# Revit family: CONV_Wexiodisk_Dishwasher_WD-4S
name_source: partatom
category: Specialty Equipment
revit_build: Autodesk Revit 2016 (Build: 20150714_1515(x64)
units: mm (PartAtom-declared; Revit-internal decimal feet)

## family parameters
Always vertical = Yes
Cut with Voids When Loaded = No
OmniClass Number = 23.45.30.14.11
OmniClass Title = Commercial Dishwashers
Part Type = Normal
Room Calculation Point = No
Round Connector Dimension = Use Diameter
Shared = No
Work Plane-Based = No

## types (1)
- WD-4S
    AssetType = Fixed
    BIMObjectName = CONV_Wexiodisk_Dishwasher_WD-4S
    BasketSize = 500x500mm
    BoosterHeater(230V) = 2800 W
    BoosterHeater(400V) = 4200 W
    BoosterPump = 370 W
    Brand = Wexiodisk
    CapacityBasketsPerHour = 50
    Category = Under-counter dishwashers
    ColdWaterConnection(5-12°C)(ExternalThread) = R3/4"
    Color = Grey
    ConvergoRefNr = 0100-1703-0001-SE
    Cost = 0 $
    DishwasherMainMaterial = Stainless Steel
    DishwasherSecondaryMaterial = Black Plastic
    DrainConnectionHose = 22.00 mm
    DrainPump = 40 W
    DurationUnit = Year
    ElectricalDeviceNominalPower = 0 W
    ExpiringDate = 12/2018
    FloorDrain = 1.0 L/s
    HasProtectiveEarth = No
    HeatLoadToRoomLatent = 500 W
    HeatLoadToRoomSensible = 1200 W
    HeatLoadToRoomTotal = 1700 W
    HeatRecoveryFan = 10 W
    HotWaterConnection(55-70°C)(ExternalThread) = R3/4"
    IP_Code = 44
    IfcExportAs = NOTDEFINED
    IfcExportType = IfcFurnitureType
    MainFuse(230V-3N) = 4 A
    MainFuse(400V-3N) = 16 A
    ManufacterURL = https://www.wexiodisk.com
    Manufacturer = Wexiodisk
    ManufacturerName = Wexiodisk
    Material = Stainless Steel
    MaximumSurfaceTemperature = 35 °C
    Model = WD-4S
    NBSDescription = Commercial undercounter dishwashers
    NBSReference = 45-35-15/424
    Name = Dishwasher_WD-4S
    NominalCurrent = 0 A
    NominalDepth = 656 mm  [stored 2.15223 ft]
    NominalFrequencyRange = 0 Hz
    NominalHeight = 820 mm  [stored 2.69029 ft]
    NominalVoltage = 0 V
    NominalWidth = 598 mm  [stored 1.96194 ft]
    NumberOfPoles = 0
    PhaseAngle = 0.00°
    Revision = 2
    Shape = Cube
    Size = 656x598x820mm
    SoundLevel = 61 dB
    TankHeater = 1400 W
    TankVolume = 20.0 L
    URL = https://www.wexiodisk.com
    Uniclass2 = Pr_40_70_21_92
    Uniclass2015Description = Under-counter dishwashers
    Uniclass2015Reference = Pr_40_70_21_92
    UsageCurrent = 0 A
    Version = 2
    VersionDate = 01/01/2018
    WarrantyDurationUnit = Year
    WashPump = 750 W
    WaterCapacityFlow = 0.8 L/s
    WaterCapacityPressure = 20000.0 Pa
    WaterConsumptionRinse/Programme = 2.4 L
    WaterQuality = 2-7 °dH
    WeightMachineInOperation = 85kg

note: [stored X ft] marks values corroborated as IEEE doubles in the binary element streams (Revit-internal decimal feet)

## geometry (parser evidence)
native form markers: Blend x4, Sweep x2
no freeform markers — native parametric forms only
